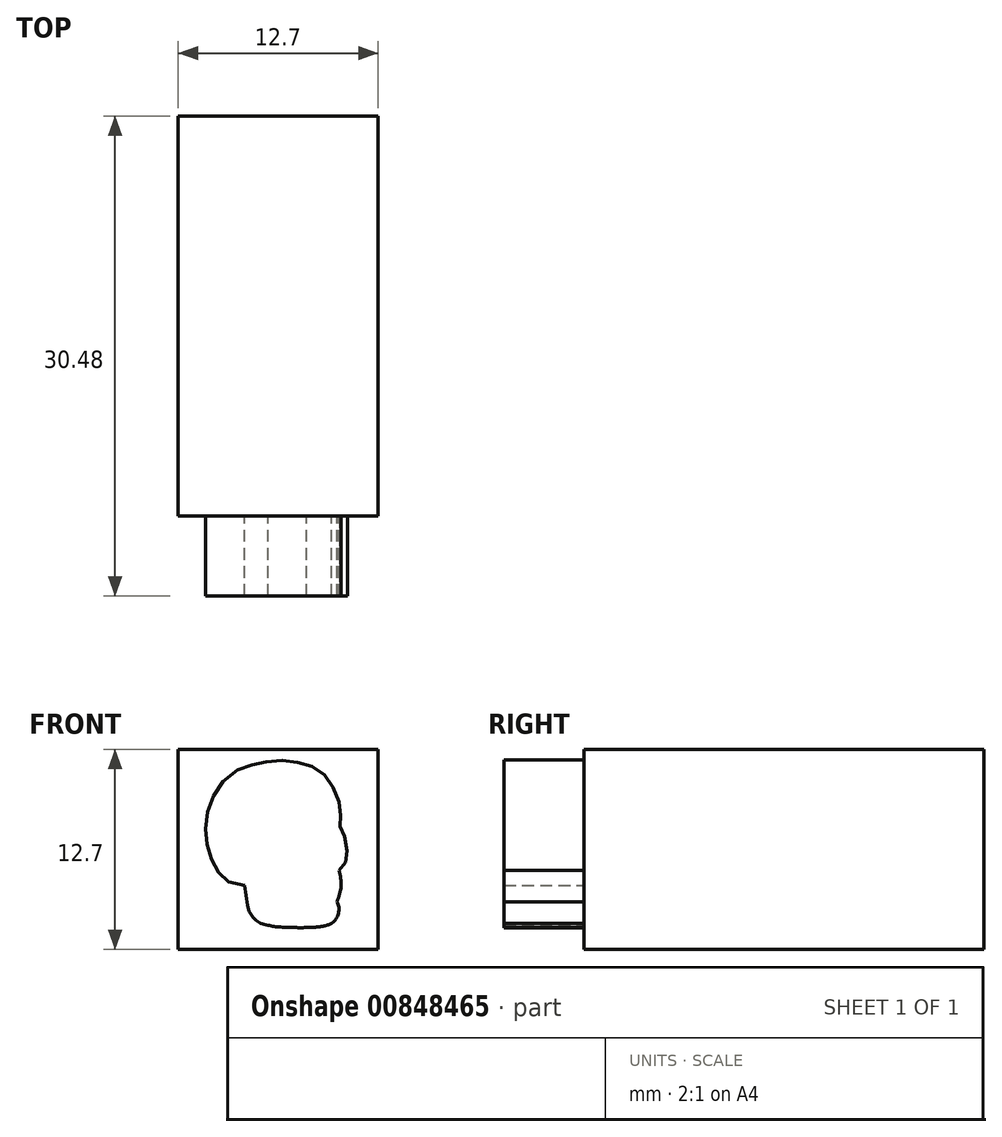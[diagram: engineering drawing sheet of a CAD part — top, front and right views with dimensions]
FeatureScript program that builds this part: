
annotation { "Feature Type Name" : "Feature", "Feature Type Description" : "" }
export const myFeature = defineFeature(function(context is Context, id is Id, definition is map)
    precondition{}
    {
        {
            var Q0;
            Q0=qCreatedBy(makeId("Front.planeOp"),FACE);
            var sketch = newSketch(context, id + "F0", { "sketchPlane" : qUnion([Q0])});
            skLineSegment(sketch, "E0", {"start": v(-8.49, 4.08) * mm, "end": v(-8.29, 2.78) * mm});
            skArc(sketch, "E1", {"start": v(-8.29, 2.78) * mm, "mid": v(-7.85, 1.94) * mm, "end": v(-7, 1.53) * mm});
            skArc(sketch, "E2", {"start": v(-2.96, 1.65) * mm, "mid": v(-2.52, 2.28) * mm, "end": v(-2.62, 3.03) * mm});
            skArc(sketch, "E3", {"start": v(-2.62, 3.03) * mm, "mid": v(-2.36, 4.02) * mm, "end": v(-2.5, 5.02) * mm});
            skFitSpline(sketch, "E4", {"points": [v(-4.55, 1.4) * mm, v(-2.96, 1.65) * mm], "startDerivative": vector(1.7, 0) * mm, "endDerivative": vector(1.51, 0.7) * mm});
            skFitSpline(sketch, "E5", {"points": [v(-7, 1.53) * mm, v(-6.47, 1.44) * mm, v(-5.8, 1.4) * mm, v(-5.14, 1.38) * mm, v(-4.55, 1.4) * mm], "startDerivative": vector(2.24, -0.47) * mm, "endDerivative": vector(2.46, 0.2) * mm});
            skFitSpline(sketch, "E6", {"points": [v(-8.49, 4.08) * mm, v(-9.51, 4.3) * mm, v(-10.06, 4.8) * mm, v(-10.44, 5.4) * mm, v(-10.8, 6.38) * mm, v(-10.93, 7.2) * mm, v(-10.93, 8.32) * mm, v(-10.58, 9.44) * mm, v(-10.08, 10.38) * mm, v(-9.1, 11.29) * mm, v(-8.17, 11.66) * mm, v(-7.5, 11.84) * mm, v(-6.48, 12.02) * mm, v(-5.53, 11.96) * mm, v(-4.6, 11.77) * mm, v(-3.86, 11.43) * mm, v(-3.19, 10.85) * mm, v(-2.74, 10.04) * mm, v(-2.44, 9.17) * mm, v(-2.38, 8.5) * mm, v(-2.47, 8) * mm, v(-2.28, 7.49) * mm, v(-2.13, 7.1) * mm, v(-1.98, 6.26) * mm, v(-2, 5.75) * mm, v(-2.21, 5.3) * mm, v(-2.5, 5.02) * mm], "startDerivative": vector(-25.63, 2.5) * mm, "endDerivative": vector(-10.88, -9.26) * mm});
            skLineSegment(sketch, "E7", {"start": v(-6.48, 12.02) * mm, "end": v(-5.14, 1.38) * mm, "construction": true});
            skSolve(sketch);
        }
        {
            var Q0;
            Q0=makeQuery(id+"F0.imprint","IMPRINT",FACE,{"disambiguationData":[TD([[makeQuery(id+"F0.imprint","IMPRINT",EDGE,{"derivedFrom":sQuery(id+"F0.wireOp",EDGE,"E0")}),1.0]])]});
            extrude(context, id + "F1", {"entities" : qUnion([Q0]), "depth" : 2.54 * mm, "offsetDistance" : 25.4 * mm});
        }
        {
            var Q0;
            Q0=qCreatedBy(makeId("Front.planeOp"),FACE);
            var sketch = newSketch(context, id + "F2", { "sketchPlane" : qUnion([Q0])});
            skLineSegment(sketch, "E8.bottom", {"start": v(0, 0) * mm, "end": v(-12.7, 0) * mm});
            skLineSegment(sketch, "E8.top", {"start": v(0, 12.7) * mm, "end": v(-12.7, 12.7) * mm});
            skLineSegment(sketch, "E8.left", {"start": v(0, 0) * mm, "end": v(0, 12.7) * mm});
            skLineSegment(sketch, "E8.right", {"start": v(-12.7, 0) * mm, "end": v(-12.7, 12.7) * mm});
            skSolve(sketch);
        }
        {
            var Q0;
            Q0=makeQuery(id+"F2.imprint","IMPRINT",FACE,{"disambiguationData":[TD([[makeQuery(id+"F2.imprint","IMPRINT",EDGE,{"derivedFrom":sQuery(id+"F2.wireOp",EDGE,"E8.bottom")}),-1.0]])]});
            extrude(context, id + "F3", {"entities" : qUnion([Q0]), "operationType" : NewBodyOperationType.ADD, "oppositeDirection" : true, "depth" : 25.4 * mm, "offsetDistance" : 25.4 * mm});
        }
        {
            var Q0;
            Q0=makeQuery(id+"F1.opExtrude","CAP_FACE",FACE,{"disambiguationData":[OSD([sQuery(id+"F0.wireOp",EDGE,"E0"),sQuery(id+"F0.wireOp",EDGE,"E1"),sQuery(id+"F0.wireOp",EDGE,"E2"),sQuery(id+"F0.wireOp",EDGE,"E3"),sQuery(id+"F0.wireOp",EDGE,"E4"),sQuery(id+"F0.wireOp",EDGE,"E5"),sQuery(id+"F0.wireOp",EDGE,"E6")])],"isStart":false});
            extrude(context, id + "F4", {"entities" : qUnion([Q0]), "operationType" : NewBodyOperationType.ADD, "depth" : 2.54 * mm, "offsetDistance" : 25.4 * mm});
        }
    });
